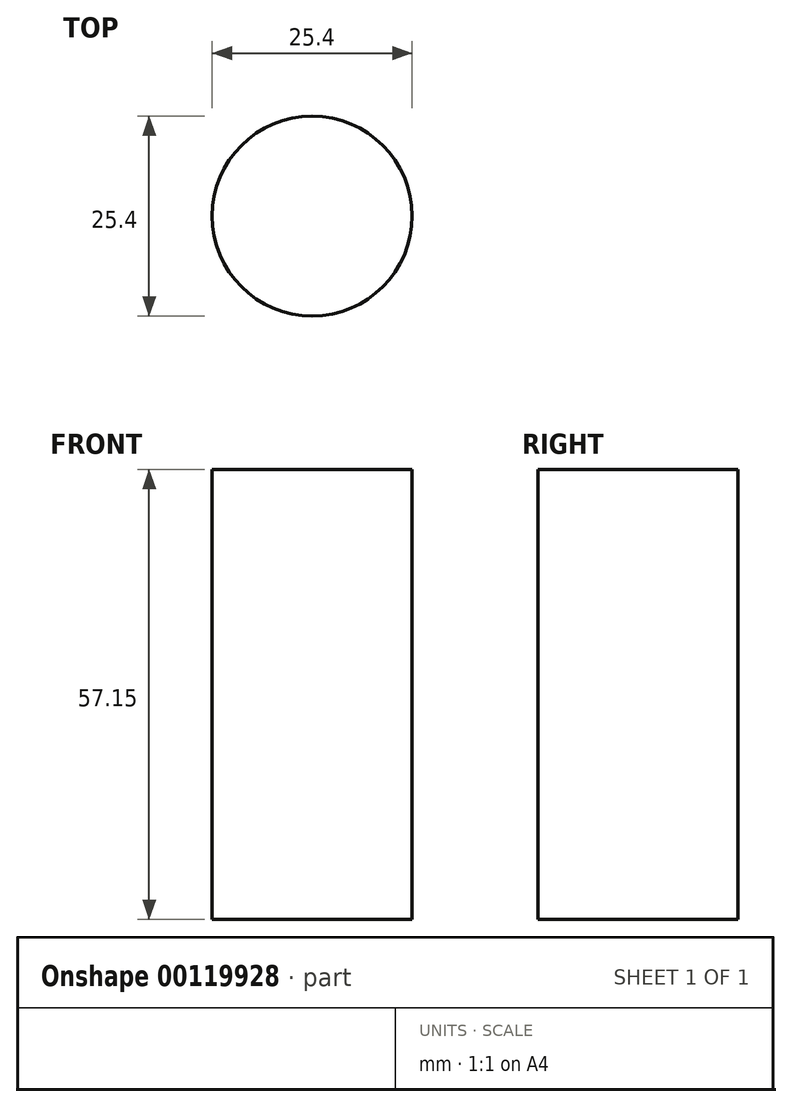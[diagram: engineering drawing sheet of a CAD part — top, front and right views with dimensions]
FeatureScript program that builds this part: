
annotation { "Feature Type Name" : "Feature", "Feature Type Description" : "" }
export const myFeature = defineFeature(function(context is Context, id is Id, definition is map)
    precondition{}
    {
        {
            var Q0;
            Q0=qCreatedBy(makeId("Top.planeOp"),FACE);
            var sketch = newSketch(context, id + "F0", { "sketchPlane" : qUnion([Q0])});
            skCircle(sketch, "E0", {"center": v(0, 0) * mm, "radius": 12.7 * mm});
            skSolve(sketch);
        }
        {
            var Q0;
            Q0=makeQuery(id+"F0.imprint","IMPRINT",FACE,{"disambiguationData":[TD([[makeQuery(id+"F0.imprint","IMPRINT",EDGE,{"derivedFrom":sQuery(id+"F0.wireOp",EDGE,"E0")}),1.0]])]});
            extrude(context, id + "F1", {"entities" : qUnion([Q0]), "depth" : 57.15 * mm});
        }
    });
